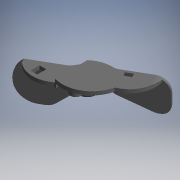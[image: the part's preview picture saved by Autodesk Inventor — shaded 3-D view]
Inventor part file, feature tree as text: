
AUTODESK INVENTOR PART (.ipt)
format: ipt  version: 2017.3 (Build 213256000, 256)  size: 246,784 bytes
history: native  units: mm (DEFAULTED — no unit token found)
features: sketch x7, other x7, extrude x6, revolve x1
ambient origin geometry x8: Origin, YZ Plane, XZ Plane, XY Plane, X Axis, Y Axis, Z Axis, Center Point
bodies: Solid1 (feature_tree)
feature tree (21):
  extrude  "Extrusion1"  Depth=50.0mm TaperAngle=0.0deg
  extrude  "Extrusion2"  Depth=2.3mm TaperAngle=0.0deg
  extrude  "Extrusion3"  Depth=2.7mm TaperAngle=0.0deg
  extrude  "Extrusion4"  TaperAngle=0.0deg  [1 undecoded]
  extrude  "Extrusion5"  [1 undecoded]
  sketch  "Sketch_7"
  extrude  "Extrusion6"  [1 undecoded]
  revolve  "Revolution1"  [1 undecoded]
  other  "stopper_to_body_XY"
  other  "stopper_to_body_YZ"
  other  "stopper_to_body_ZX"
  other  "stopper_to_body_X"
  other  "stopper_to_body_Y"
  other  "stopper_to_body_Z"
  other  "stopper_to_body_Center"
  sketch  "Sketch_1"  dims[d0=25.0mm d1=0.0mm d2=50.0mm d3=0.0mm]
  sketch  "Sketch_2"  dims[d4=50.0mm d5=0.0mm d6=2.3mm d7=0.0mm]
  sketch  "Sketch_8"
  sketch  "Sketch_9"
  sketch  "Sketch_3"  dims[d8=100.0mm d9=0.0mm d10=2.7mm d11=0.0mm]
  sketch  "Sketch_4"  dims[d12=360.0deg d13=0.0mm]
note: 4 required parameter values undecoded (feature->parameter linkage not recoverable at this tier; creation-order binding heuristic only, values carry confidence <= 0.55)
